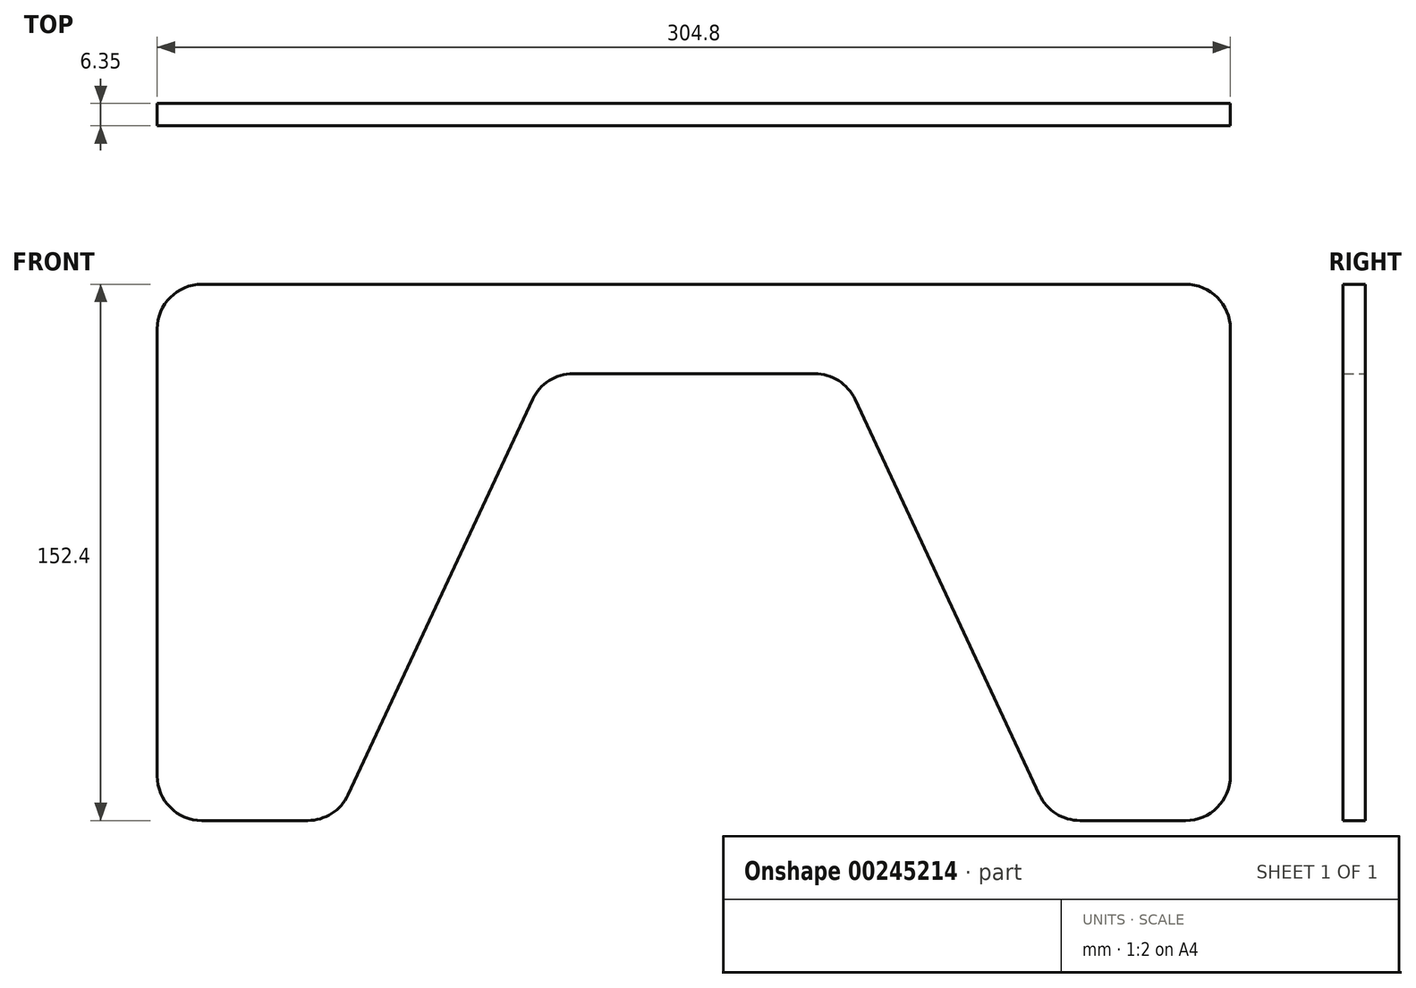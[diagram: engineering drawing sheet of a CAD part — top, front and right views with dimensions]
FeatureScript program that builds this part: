
annotation { "Feature Type Name" : "Feature", "Feature Type Description" : "" }
export const myFeature = defineFeature(function(context is Context, id is Id, definition is map)
    precondition{}
    {
        {
            var Q0;
            Q0=qCreatedBy(makeId("Front.planeOp"),FACE);
            var sketch = newSketch(context, id + "F0", { "sketchPlane" : qUnion([Q0])});
            skLineSegment(sketch, "E0.bottom", {"start": v(-76.2, 76.2) * mm, "end": v(76.2, 76.2) * mm});
            skLineSegment(sketch, "E0.top", {"start": v(-76.2, -76.2) * mm, "end": v(76.2, -76.2) * mm});
            skLineSegment(sketch, "E0.left", {"start": v(-76.2, 76.2) * mm, "end": v(-76.2, -76.2) * mm});
            skLineSegment(sketch, "E0.right", {"start": v(76.2, 76.2) * mm, "end": v(76.2, -76.2) * mm});
            skPoint(sketch, "E0.middle", {"position": v(0, 0) * mm});
            skLineSegment(sketch, "E1", {"start": v(-76.2, -76.2) * mm, "end": v(-25.4, -76.2) * mm});
            skLineSegment(sketch, "E2", {"start": v(-25.4, -76.2) * mm, "end": v(33.82, 50.8) * mm});
            skLineSegment(sketch, "E3", {"start": v(33.82, 50.8) * mm, "end": v(76.2, 50.8) * mm});
            skSolve(sketch);
        }
        {
            var Q0;
            {var subQ1=sQuery(id+"F0.wireOp",EDGE,"E0.bottom");Q0=makeQuery(id+"F0.imprint","IMPRINT",FACE,{"disambiguationData":[TD([[makeQuery(id+"F0.imprint","IMPRINT",EDGE,{"derivedFrom":subQ1}),-1.0]])]});}
            extrude(context, id + "F1", {"entities" : qUnion([Q0]), "depth" : 6.35 * mm});
        }
        {
            var Q0;
            Q0=makeQuery(id+"F1.opExtrude","SWEPT_BODY",BODY,{"disambiguationData":[OSD([sQuery(id+"F0.wireOp",EDGE,"E0.bottom"),sQuery(id+"F0.wireOp",EDGE,"E0.left"),sQuery(id+"F0.wireOp",EDGE,"E0.right"),sQuery(id+"F0.wireOp",EDGE,"E1"),sQuery(id+"F0.wireOp",EDGE,"E2"),sQuery(id+"F0.wireOp",EDGE,"E3")])]});
            var Q1;
            Q1=makeQuery(id+"F1.opExtrude","SWEPT_FACE",FACE,{"disambiguationData":[OSD([sQuery(id+"F0.wireOp",EDGE,"E0.right")])]});
            mirror(context, id + "F2", {"operationType" : NewBodyOperationType.ADD, "entities" : qUnion([Q0]), "mirrorPlane" : qUnion([Q1])});
        }
        {
            var Q0;
            Q0=makeQuery(id+"F1.opExtrude","SWEPT_EDGE",EDGE,{"disambiguationData":[OSD([sQuery(id+"F0.wireOp",EDGE,"E2"),sQuery(id+"F0.wireOp",EDGE,"E3")])]});
            var Q1;
            Q1=makeQuery(id+"F2.opPattern","COPY",EDGE,{"derivedFrom":makeQuery(id+"F1.opExtrude","SWEPT_EDGE",EDGE,{"disambiguationData":[OSD([sQuery(id+"F0.wireOp",EDGE,"E2"),sQuery(id+"F0.wireOp",EDGE,"E3")])]}),"instanceName":"1"});
            var Q2;
            Q2=makeQuery(id+"F2.opPattern","COPY",EDGE,{"derivedFrom":makeQuery(id+"F1.opExtrude","SWEPT_EDGE",EDGE,{"disambiguationData":[OSD([sQuery(id+"F0.wireOp",EDGE,"E0.top"),sQuery(id+"F0.wireOp",EDGE,"E1"),sQuery(id+"F0.wireOp",EDGE,"E2")])]}),"instanceName":"1"});
            var Q3;
            Q3=makeQuery(id+"F1.opExtrude","SWEPT_EDGE",EDGE,{"disambiguationData":[OSD([sQuery(id+"F0.wireOp",EDGE,"E0.top"),sQuery(id+"F0.wireOp",EDGE,"E1"),sQuery(id+"F0.wireOp",EDGE,"E2")])]});
            var Q4;
            Q4=makeQuery(id+"F1.opExtrude","SWEPT_EDGE",EDGE,{"disambiguationData":[OSD([sQuery(id+"F0.wireOp",EDGE,"E0.left"),sQuery(id+"F0.wireOp",EDGE,"E1")])]});
            var Q5;
            Q5=makeQuery(id+"F2.opPattern","COPY",EDGE,{"derivedFrom":makeQuery(id+"F1.opExtrude","SWEPT_EDGE",EDGE,{"disambiguationData":[OSD([sQuery(id+"F0.wireOp",EDGE,"E0.left"),sQuery(id+"F0.wireOp",EDGE,"E1")])]}),"instanceName":"1"});
            var Q6;
            Q6=makeQuery(id+"F2.opPattern","COPY",EDGE,{"derivedFrom":makeQuery(id+"F1.opExtrude","SWEPT_EDGE",EDGE,{"disambiguationData":[OSD([sQuery(id+"F0.wireOp",EDGE,"E0.bottom"),sQuery(id+"F0.wireOp",EDGE,"E0.left")])]}),"instanceName":"1"});
            var Q7;
            Q7=makeQuery(id+"F1.opExtrude","SWEPT_EDGE",EDGE,{"disambiguationData":[OSD([sQuery(id+"F0.wireOp",EDGE,"E0.bottom"),sQuery(id+"F0.wireOp",EDGE,"E0.left")])]});
            fillet(context, id + "F3", {"entities" : qUnion([Q0, Q1, Q2, Q3, Q4, Q5, Q6, Q7]), "radius" : 12.7 * mm, "tangentPropagation" : true, "allowEdgeOverflow" : false});
        }
    });
